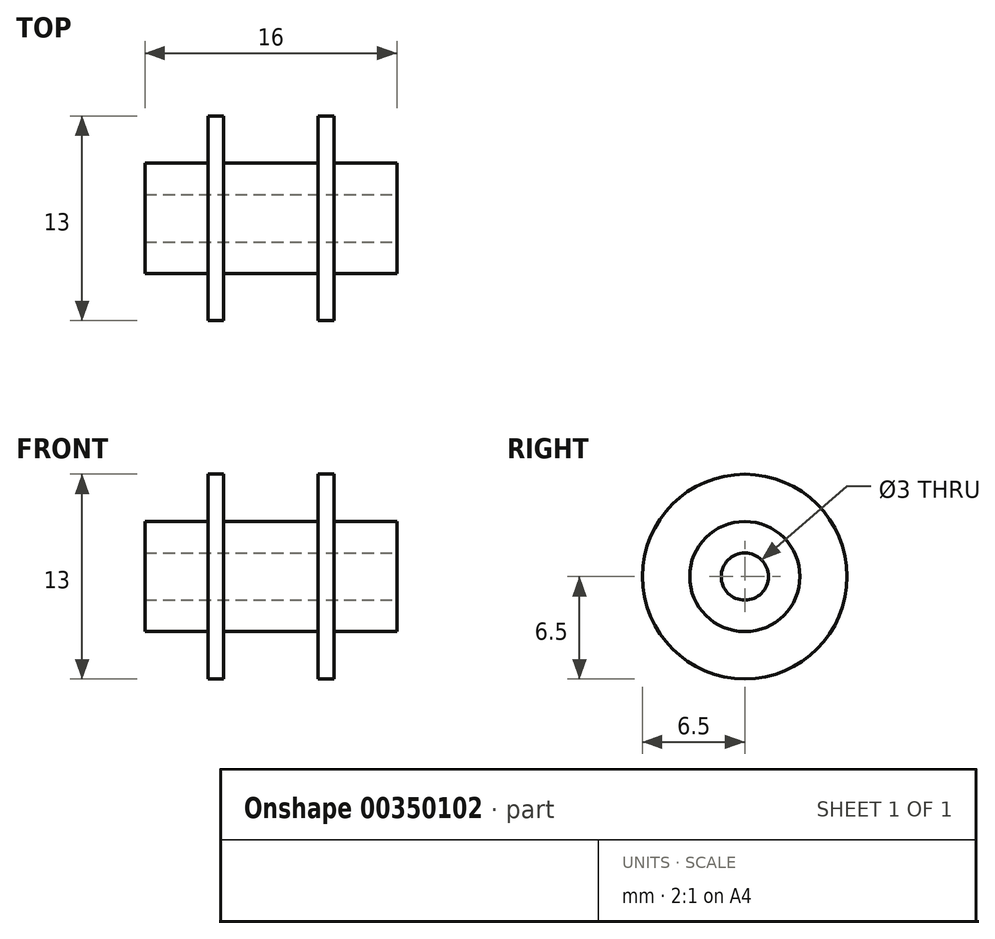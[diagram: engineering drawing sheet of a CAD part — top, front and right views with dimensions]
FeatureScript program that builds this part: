
annotation { "Feature Type Name" : "Feature", "Feature Type Description" : "" }
export const myFeature = defineFeature(function(context is Context, id is Id, definition is map)
    precondition{}
    {
        {
            var Q0;
            Q0=qCreatedBy(makeId("Front.planeOp"),FACE);
            var sketch = newSketch(context, id + "F0", { "sketchPlane" : qUnion([Q0])});
            skLineSegment(sketch, "E0", {"start": v(0, 0) * mm, "end": v(0, 1.5) * mm, "construction": true});
            skLineSegment(sketch, "E1", {"start": v(0, 0) * mm, "end": v(-31.32, 0) * mm, "construction": true});
            skLineSegment(sketch, "E2", {"start": v(0, 1.5) * mm, "end": v(8, 1.5) * mm});
            skLineSegment(sketch, "E3", {"start": v(8, 1.5) * mm, "end": v(8, 3.5) * mm});
            skLineSegment(sketch, "E4", {"start": v(8, 3.5) * mm, "end": v(4, 3.5) * mm});
            skLineSegment(sketch, "E5", {"start": v(4, 3.5) * mm, "end": v(4, 6.5) * mm});
            skLineSegment(sketch, "E6", {"start": v(4, 6.5) * mm, "end": v(3, 6.5) * mm});
            skLineSegment(sketch, "E7", {"start": v(3, 6.5) * mm, "end": v(3, 3.5) * mm});
            skLineSegment(sketch, "E8", {"start": v(3, 3.5) * mm, "end": v(0, 3.5) * mm});
            skLineSegment(sketch, "E9", {"start": v(0, 0) * mm, "end": v(0, 12.7) * mm, "construction": true});
            skLineSegment(sketch, "E10.MirrorCS", {"start": v(-4, 6.5) * mm, "end": v(-3, 6.5) * mm});
            skLineSegment(sketch, "E11.MirrorCS", {"start": v(-8, 1.5) * mm, "end": v(-8, 3.5) * mm});
            skLineSegment(sketch, "E12.MirrorCS", {"start": v(-3, 3.5) * mm, "end": v(0, 3.5) * mm});
            skLineSegment(sketch, "E13.MirrorCS", {"start": v(-3, 6.5) * mm, "end": v(-3, 3.5) * mm});
            skLineSegment(sketch, "E14.MirrorCS", {"start": v(0, 1.5) * mm, "end": v(-8, 1.5) * mm});
            skLineSegment(sketch, "E15.MirrorCS", {"start": v(-4, 3.5) * mm, "end": v(-4, 6.5) * mm});
            skLineSegment(sketch, "E16.MirrorCS", {"start": v(-8, 3.5) * mm, "end": v(-4, 3.5) * mm});
            skSolve(sketch);
        }
        {
            var Q0;
            Q0=makeQuery(id+"F0.imprint","IMPRINT",FACE,{"disambiguationData":[TD([[makeQuery(id+"F0.imprint","IMPRINT",EDGE,{"derivedFrom":sQuery(id+"F0.wireOp",EDGE,"E2")}),1.0]])]});
            var Q1;
            Q1=sQuery(id+"F0.wireOp",EDGE,"E1");
            revolve(context, id + "F1", {"entities" : qUnion([Q0]), "axis" : qUnion([Q1]), "revolveType" : RevolveType.FULL});
        }
    });
